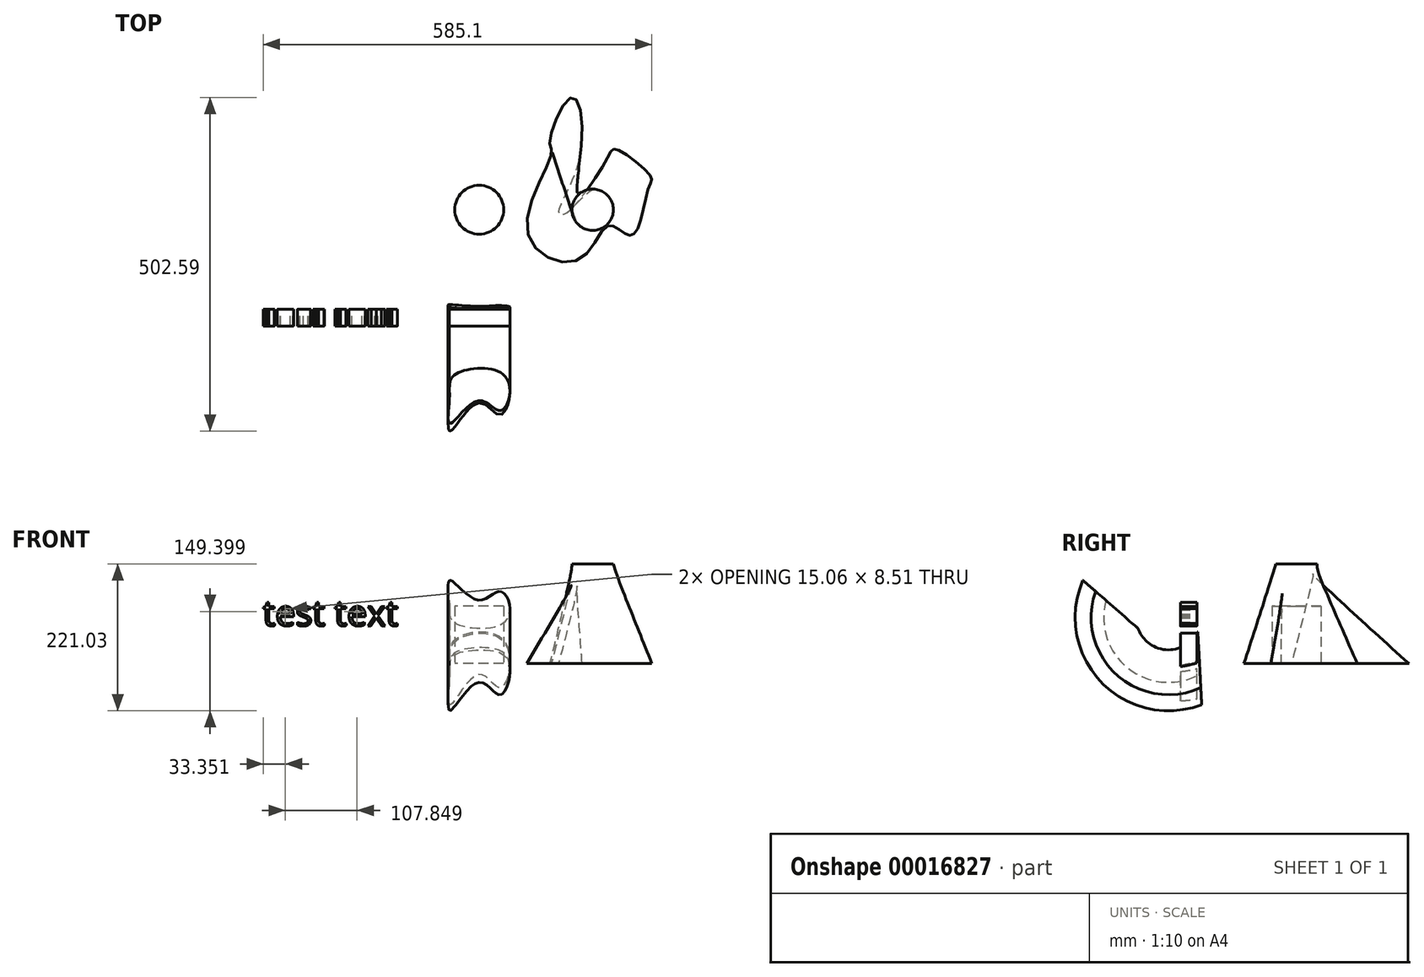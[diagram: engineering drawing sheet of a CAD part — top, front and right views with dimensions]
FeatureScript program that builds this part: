
annotation { "Feature Type Name" : "Feature", "Feature Type Description" : "" }
export const myFeature = defineFeature(function(context is Context, id is Id, definition is map)
    precondition{}
    {
        {
            var Q0;
            Q0=qCreatedBy(makeId("Top.planeOp"),FACE);
            var sketch = newSketch(context, id + "F0", { "sketchPlane" : qUnion([Q0])});
            skCircle(sketch, "E0", {"center": v(0, 0) * mm, "radius": 36.83 * mm});
            skSolve(sketch);
        }
        {
            var Q0;
            Q0=makeQuery(id+"F0.imprint","IMPRINT",FACE,{"disambiguationData":[TD([[makeQuery(id+"F0.imprint","IMPRINT",EDGE,{"derivedFrom":sQuery(id+"F0.wireOp",EDGE,"E0")}),1.0]])]});
            var Q1;
            Q1=sQuery(id+"F0.wireOp",EDGE,"E0");
            extrude(context, id + "F1", {"entities" : qUnion([Q0]), "surfaceEntities" : qUnion([Q1]), "depth" : 86.24 * mm});
        }
        {
            var Q0;
            Q0=makeQuery(id+"F1.opExtrude","CAP_FACE",FACE,{"disambiguationData":[OSD([sQuery(id+"F0.wireOp",EDGE,"E0")])],"isStart":false});
            var sketch = newSketch(context, id + "F2", { "sketchPlane" : qUnion([Q0])});
            skCircle(sketch, "E1.cCircle", {"center": v(0, 0) * mm, "radius": 19.21 * mm, "construction": true});
            skLineSegment(sketch, "E1.0", {"start": v(12.93, 16.29) * mm, "end": v(20.66, 2.38) * mm});
            skLineSegment(sketch, "E1.1", {"start": v(20.66, 2.38) * mm, "end": v(16.29, -12.93) * mm});
            skLineSegment(sketch, "E1.2", {"start": v(16.29, -12.93) * mm, "end": v(2.38, -20.66) * mm});
            skLineSegment(sketch, "E1.3", {"start": v(2.38, -20.66) * mm, "end": v(-12.93, -16.29) * mm});
            skLineSegment(sketch, "E1.4", {"start": v(-12.93, -16.29) * mm, "end": v(-20.66, -2.38) * mm});
            skLineSegment(sketch, "E1.5", {"start": v(-20.66, -2.38) * mm, "end": v(-16.29, 12.93) * mm});
            skLineSegment(sketch, "E1.6", {"start": v(-16.29, 12.93) * mm, "end": v(-2.38, 20.66) * mm});
            skLineSegment(sketch, "E1.7", {"start": v(-2.38, 20.66) * mm, "end": v(12.93, 16.29) * mm});
            skPoint(sketch, "E1.0.midPoint", {"position": v(16.8, 9.33) * mm});
            skSolve(sketch);
        }
        {
            var Q0;
            Q0 = qSketchRegion(id + "F2", true);
            var Q1;
            Q1 = qConstructionFilter(qBodyType(qCreatedBy(id + "F2" ,EDGE), BodyType.WIRE), ConstructionObject.NO);
            extrude(context, id + "F3", {"entities" : qUnion([Q0]), "bodyType" : ToolBodyType.SURFACE, "surfaceEntities" : qUnion([Q1]), "depth" : 45.3 * mm});
        }
        {
            var Q0;
            Q0=qCreatedBy(makeId("Top.planeOp"),FACE);
            var sketch = newSketch(context, id + "F4", { "sketchPlane" : qUnion([Q0])});
            skFitSpline(sketch, "E2", {"points": [v(193.66, -24.29) * mm, v(149.04, -75.6) * mm, v(73.14, -35.21) * mm, v(108.55, 84.11) * mm, v(106.13, 102.98) * mm, v(139.6, 169.15) * mm, v(150.34, 75.96) * mm, v(119.66, -4.3) * mm, v(129.7, -5.7) * mm, v(194.36, 80.01) * mm, v(206.19, 91.2) * mm, v(258.73, 49.72) * mm, v(255.74, 35.02) * mm, v(235.97, -33.28) * mm, v(220.85, -36.6) * mm, v(193.66, -24.29) * mm]});
            skSolve(sketch);
        }
        {
            var Q0;
            Q0=qCreatedBy(makeId("Top.planeOp"),FACE);
            cPlane(context, id + "F5", {"entities" : qUnion([Q0]), "cplaneType" : CPlaneType.OFFSET, "offset" : 150 * mm, "width" : 150 * mm, "height" : 150 * mm});
        }
        {
            var Q0;
            Q0=qCreatedBy(id+"F5.planeOp",FACE);
            var sketch = newSketch(context, id + "F6", { "sketchPlane" : qUnion([Q0])});
            skCircle(sketch, "E3", {"center": v(170.82, 0) * mm, "radius": 31.13 * mm});
            skSolve(sketch);
        }
        {
            var Q0;
            Q0=makeQuery(id+"F4.imprint","IMPRINT",FACE,{"disambiguationData":[TD([[makeQuery(id+"F4.imprint","IMPRINT",EDGE,{"derivedFrom":sQuery(id+"F4.wireOp",EDGE,"E2")}),-1.0]])]});
            var Q1;
            Q1=makeQuery(id+"F6.imprint","IMPRINT",FACE,{"disambiguationData":[TD([[makeQuery(id+"F6.imprint","IMPRINT",EDGE,{"derivedFrom":sQuery(id+"F6.wireOp",EDGE,"E3")}),1.0]])]});
            loft(context, id + "F7", {"sheetProfilesArray" : [{ "sheetProfileEntities" : qUnion([Q0]) }, { "sheetProfileEntities" : qUnion([Q1]) }]});
        }
        {
            var Q0;
            Q0=qCreatedBy(makeId("Front.planeOp"),FACE);
            cPlane(context, id + "F8", {"entities" : qUnion([Q0]), "cplaneType" : CPlaneType.OFFSET, "offset" : 150 * mm, "width" : 150 * mm, "height" : 150 * mm});
        }
        {
            var Q0;
            Q0=qCreatedBy(id+"F8.planeOp",FACE);
            var sketch = newSketch(context, id + "F9", { "sketchPlane" : qUnion([Q0])});
            skFitSpline(sketch, "E4", {"points": [v(-44.82, -13.23) * mm, v(-34.01, 35.39) * mm, v(38.64, 30.44) * mm, v(31.53, -38.8) * mm, v(0, -18.55) * mm, v(-43.38, -64.3) * mm, v(-44.82, -13.23) * mm]});
            skText(sketch, "E5", { "text": "test text", "fontName": "OpenSans-Regular.ttf"});
            const initialGuessF9  = {"E5": [-0.32598, 0.05695, 1, 0, 0.03875]};
            skSetInitialGuess(sketch, initialGuessF9);
            skSolve(sketch);
        }
        {
            var Q0;
            Q0=qCreatedBy(makeId("Right.planeOp"),FACE);
            var sketch = newSketch(context, id + "F10", { "sketchPlane" : qUnion([Q0])});
            skArc(sketch, "E6", {"start": v(-275.08, 84.72) * mm, "mid": v(-238.7, -0.37) * mm, "end": v(-146.17, 0) * mm});
            skSolve(sketch);
        }
        {
            var Q0;
            Q0=makeQuery(id+"F9.imprint","IMPRINT",FACE,{"disambiguationData":[TD([[makeQuery(id+"F9.imprint","IMPRINT",EDGE,{"derivedFrom":sQuery(id+"F9.wireOp",EDGE,"E4")}),-1.0]])]});
            var Q1;
            Q1=sQuery(id+"F9.wireOp",EDGE,"E4");
            var Q2;
            Q2=sQuery(id+"F10.wireOp",EDGE,"E6");
            sweep(context, id + "F11", {"profiles" : qUnion([Q0]), "surfaceProfiles" : qUnion([Q1]), "path" : qUnion([Q2])});
        }
        {
            var Q0;
            Q0 = qSketchRegion(id + "F9", true);
            extrude(context, id + "F12", {"entities" : qUnion([Q0]), "operationType" : NewBodyOperationType.ADD, "depth" : 25 * mm});
        }
    });
